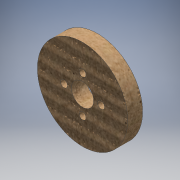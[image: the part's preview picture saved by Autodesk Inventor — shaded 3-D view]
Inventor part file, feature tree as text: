
AUTODESK INVENTOR PART (.ipt)
format: ipt  version: 2016 (Build 200138000, 138)  size: 153,600 bytes
history: native  units: mm
features: extrude x1, sketch x1
ambient origin geometry x8: Origin, YZ Plane, XZ Plane, XY Plane, X Axis, Y Axis, Z Axis, Center Point
bodies: Solid1 (feature_tree)
feature tree (2):
  extrude  "Extrusion1"  Depth=6.39mm TaperAngle=360.0deg
  sketch  "Sketch1"  dims[d0=38.592635mm d3=40.0mm d5=360.0deg d7=9.525mm d8=6.39mm d9=0.0mm]
